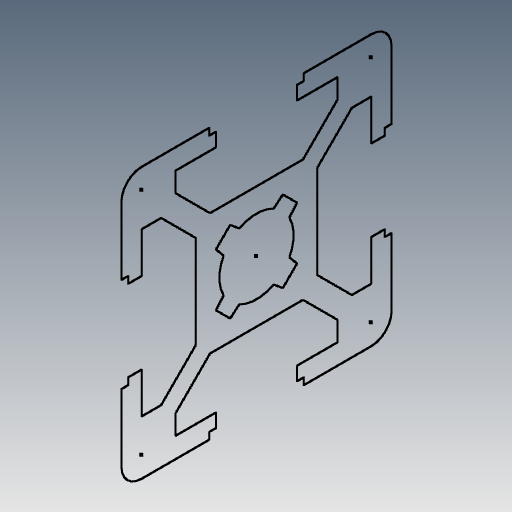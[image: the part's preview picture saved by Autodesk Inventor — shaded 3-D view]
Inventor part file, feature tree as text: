
AUTODESK INVENTOR PART (.ipt)
format: ipt  version: 2018.2 (Build 222227000, 227)  size: 102,912 bytes
history: native  units: mm
features: sketch x2, other x1
ambient origin geometry x8: Origin, YZ Plane, XZ Plane, XY Plane, X Axis, Y Axis, Z Axis, Center Point
feature tree (3):
  other  "90-50-PROFILES-20x20xSketch_AA.ipt"
  sketch  "Skizze4"
  sketch  "Skizze2"  dims[d2=10.0mm]
